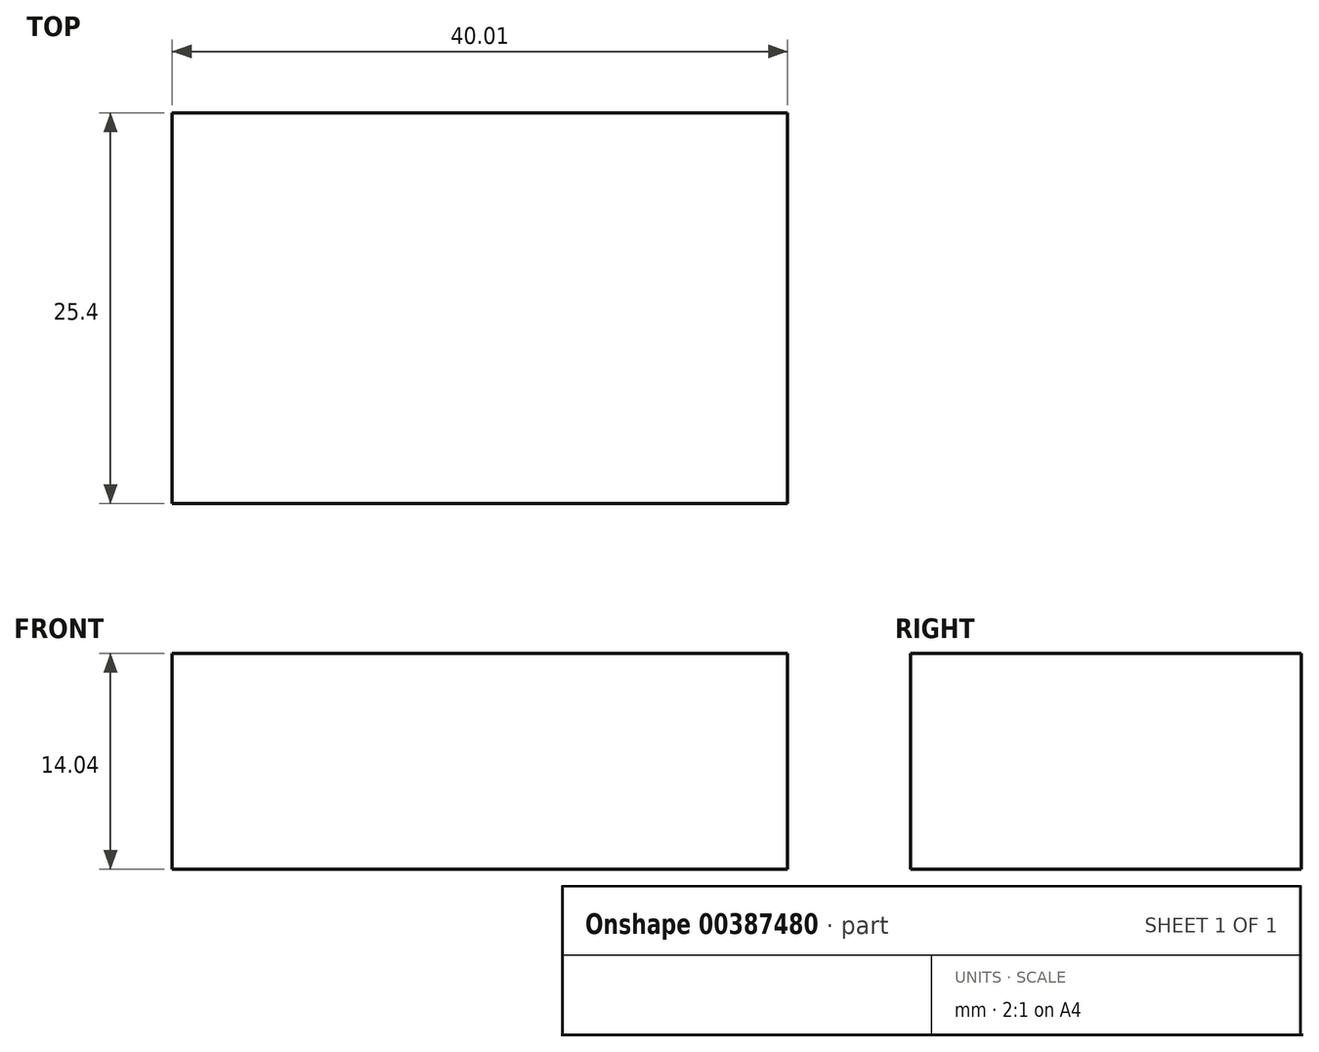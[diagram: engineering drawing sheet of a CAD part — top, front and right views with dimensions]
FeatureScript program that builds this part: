
annotation { "Feature Type Name" : "Feature", "Feature Type Description" : "" }
export const myFeature = defineFeature(function(context is Context, id is Id, definition is map)
    precondition{}
    {
        {
            var Q0;
            Q0=qCreatedBy(makeId("Front.planeOp"),FACE);
            var sketch = newSketch(context, id + "F0", { "sketchPlane" : qUnion([Q0])});
            skCircle(sketch, "E0", {"center": v(0, 0) * mm, "radius": 2.5 * mm});
            skLineSegment(sketch, "E1", {"start": v(8.27, 3.31) * mm, "end": v(12.02, 0) * mm});
            skLineSegment(sketch, "E2", {"start": v(12.02, 0) * mm, "end": v(12.02, -31.69) * mm});
            skLineSegment(sketch, "E3", {"start": v(12.02, -31.69) * mm, "end": v(-27.99, -31.69) * mm});
            skLineSegment(sketch, "E4", {"start": v(8.27, 3.31) * mm, "end": v(-27.99, 3.31) * mm});
            skLineSegment(sketch, "E5", {"start": v(-27.99, 3.31) * mm, "end": v(-27.99, -31.69) * mm});
            skLineSegment(sketch, "E6", {"start": v(-27.99, -17.65) * mm, "end": v(12.02, -17.65) * mm});
            skSolve(sketch);
        }
        {
            var Q0;
            {var subQ0=sQuery(id+"F0.wireOp",EDGE,"E3");Q0=makeQuery(id+"F0.imprint","IMPRINT",FACE,{"disambiguationData":[TD([[makeQuery(id+"F0.imprint","IMPRINT",EDGE,{"derivedFrom":subQ0}),-1.0]])]});}
            extrude(context, id + "F1", {"entities" : qUnion([Q0]), "depth" : 25.4 * mm});
        }
    });
